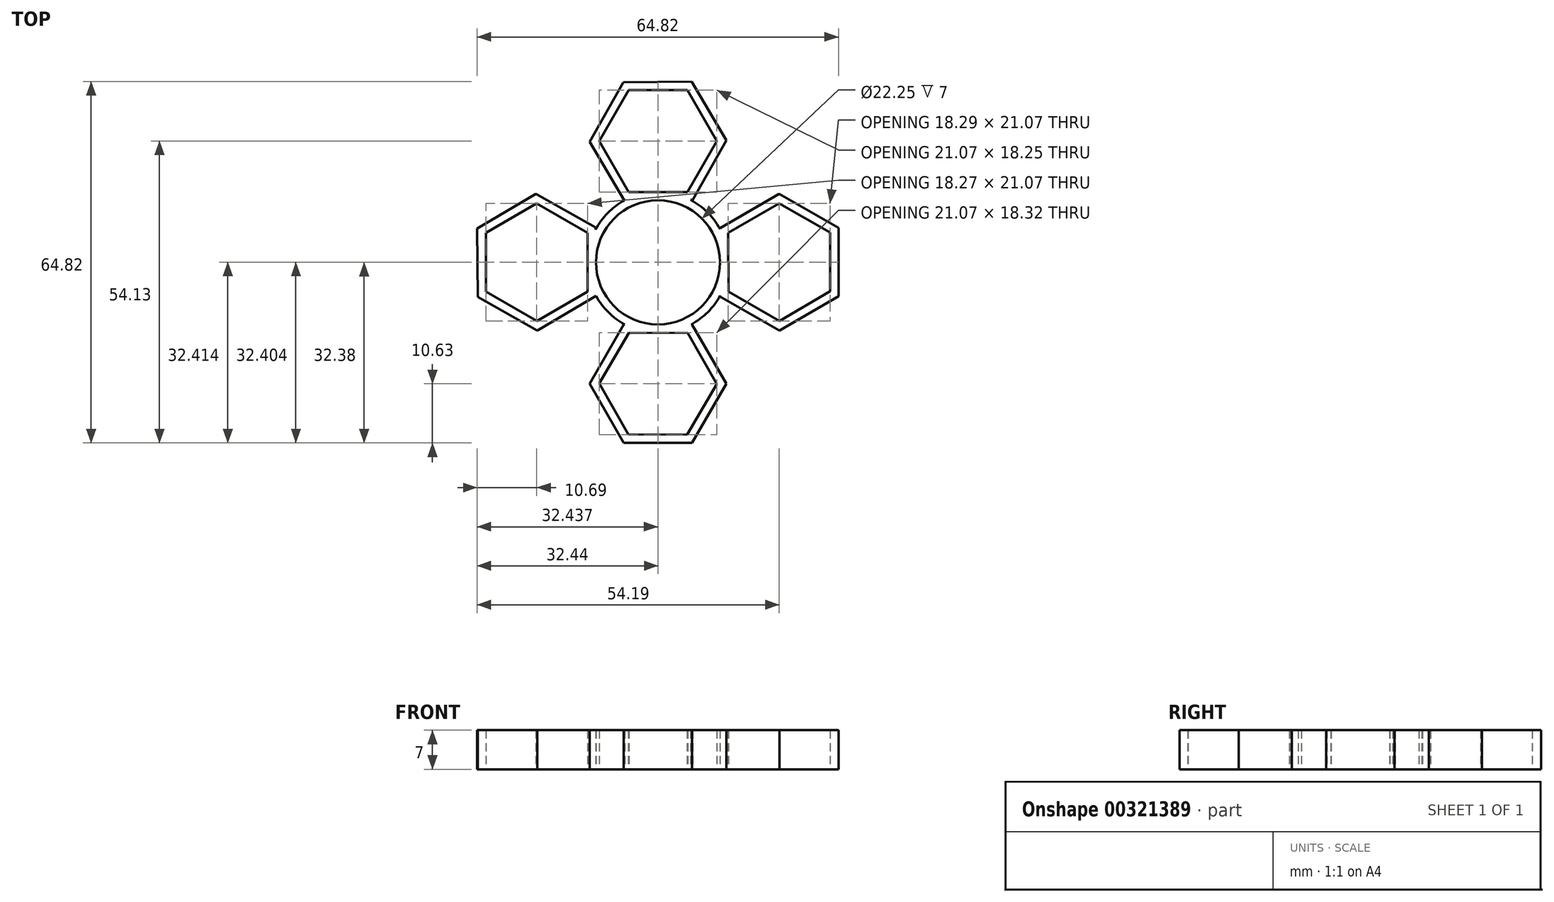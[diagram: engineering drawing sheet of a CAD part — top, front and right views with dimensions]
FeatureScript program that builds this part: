
annotation { "Feature Type Name" : "Feature", "Feature Type Description" : "" }
export const myFeature = defineFeature(function(context is Context, id is Id, definition is map)
    precondition{}
    {
        {
            var Q0;
            Q0=qCreatedBy(makeId("Top.planeOp"),FACE);
            var sketch = newSketch(context, id + "F0", { "sketchPlane" : qUnion([Q0])});
            skCircle(sketch, "E0", {"center": v(0, 0) * mm, "radius": 11.12 * mm});
            skCircle(sketch, "E1", {"center": v(0, 0) * mm, "radius": 12.62 * mm});
            skPoint(sketch, "E2", {"position": v(0, 12.63) * mm});
            skPoint(sketch, "E3", {"position": v(0, 21.75) * mm});
            skCircle(sketch, "E4", {"center": v(0, 21.75) * mm, "radius": 9.12 * mm, "construction": true});
            skPoint(sketch, "E5", {"position": v(0.1, 11.12) * mm});
            skLineSegment(sketch, "E6.0", {"start": v(5.27, 12.63) * mm, "end": v(-5.27, 12.63) * mm});
            skLineSegment(sketch, "E6.1", {"start": v(-5.27, 12.63) * mm, "end": v(-10.54, 21.75) * mm});
            skLineSegment(sketch, "E6.2", {"start": v(-10.54, 21.75) * mm, "end": v(-5.27, 30.88) * mm});
            skLineSegment(sketch, "E6.3", {"start": v(-5.27, 30.88) * mm, "end": v(5.27, 30.88) * mm});
            skLineSegment(sketch, "E6.4", {"start": v(5.27, 30.88) * mm, "end": v(10.54, 21.75) * mm});
            skLineSegment(sketch, "E6.5", {"start": v(10.54, 21.75) * mm, "end": v(5.27, 12.63) * mm});
            skCircle(sketch, "E7.cCircle", {"center": v(0, 21.75) * mm, "radius": 10.63 * mm, "construction": true});
            skLineSegment(sketch, "E7.0", {"start": v(6.24, 11.19) * mm, "end": v(-6.03, 11.06) * mm});
            skLineSegment(sketch, "E7.1", {"start": v(-6.03, 11.06) * mm, "end": v(-12.27, 21.63) * mm});
            skLineSegment(sketch, "E7.2", {"start": v(-12.27, 21.63) * mm, "end": v(-6.24, 32.31) * mm});
            skLineSegment(sketch, "E7.3", {"start": v(-6.24, 32.31) * mm, "end": v(6.03, 32.44) * mm});
            skLineSegment(sketch, "E7.4", {"start": v(6.03, 32.44) * mm, "end": v(12.27, 21.87) * mm});
            skLineSegment(sketch, "E7.5", {"start": v(12.27, 21.87) * mm, "end": v(6.24, 11.19) * mm});
            skPoint(sketch, "E8", {"position": v(11.12, 0.02) * mm});
            skPoint(sketch, "E9", {"position": v(12.62, 0) * mm});
            skPoint(sketch, "E10", {"position": v(21.75, 0.03) * mm});
            skCircle(sketch, "E11", {"center": v(21.75, 0.03) * mm, "radius": 9.13 * mm, "construction": true});
            skLineSegment(sketch, "E12.0", {"start": v(12.64, -5.27) * mm, "end": v(12.6, 5.27) * mm});
            skLineSegment(sketch, "E12.1", {"start": v(12.6, 5.27) * mm, "end": v(21.71, 10.57) * mm});
            skLineSegment(sketch, "E12.2", {"start": v(21.71, 10.57) * mm, "end": v(30.86, 5.34) * mm});
            skLineSegment(sketch, "E12.3", {"start": v(30.86, 5.34) * mm, "end": v(30.9, -5.2) * mm});
            skLineSegment(sketch, "E12.4", {"start": v(30.9, -5.2) * mm, "end": v(21.79, -10.5) * mm});
            skLineSegment(sketch, "E12.5", {"start": v(21.79, -10.5) * mm, "end": v(12.64, -5.27) * mm});
            skCircle(sketch, "E13.cCircle", {"center": v(21.75, 0.03) * mm, "radius": 10.63 * mm, "construction": true});
            skLineSegment(sketch, "E13.0", {"start": v(11.13, -6.12) * mm, "end": v(11.12, 6.15) * mm});
            skLineSegment(sketch, "E13.1", {"start": v(11.12, 6.15) * mm, "end": v(21.73, 12.3) * mm});
            skLineSegment(sketch, "E13.2", {"start": v(21.73, 12.3) * mm, "end": v(32.37, 6.19) * mm});
            skLineSegment(sketch, "E13.3", {"start": v(32.37, 6.19) * mm, "end": v(32.38, -6.08) * mm});
            skLineSegment(sketch, "E13.4", {"start": v(32.38, -6.08) * mm, "end": v(21.77, -12.23) * mm});
            skLineSegment(sketch, "E13.5", {"start": v(21.77, -12.23) * mm, "end": v(11.13, -6.12) * mm});
            skPoint(sketch, "E14", {"position": v(0, -11.12) * mm});
            skPoint(sketch, "E15", {"position": v(0.06, -12.62) * mm});
            skPoint(sketch, "E16", {"position": v(0, -21.75) * mm});
            skCircle(sketch, "E17", {"center": v(0, -21.75) * mm, "radius": 9.12 * mm, "construction": true});
            skCircle(sketch, "E18.cCircle", {"center": v(0, -21.75) * mm, "radius": 9.13 * mm, "construction": true});
            skLineSegment(sketch, "E18.0", {"start": v(-5.2, -12.59) * mm, "end": v(5.33, -12.66) * mm});
            skLineSegment(sketch, "E18.1", {"start": v(5.33, -12.66) * mm, "end": v(10.53, -21.82) * mm});
            skLineSegment(sketch, "E18.2", {"start": v(10.53, -21.82) * mm, "end": v(5.2, -30.91) * mm});
            skLineSegment(sketch, "E18.3", {"start": v(5.2, -30.91) * mm, "end": v(-5.33, -30.84) * mm});
            skLineSegment(sketch, "E18.4", {"start": v(-5.33, -30.84) * mm, "end": v(-10.54, -21.68) * mm});
            skLineSegment(sketch, "E18.5", {"start": v(-10.54, -21.68) * mm, "end": v(-5.2, -12.59) * mm});
            skCircle(sketch, "E19.cCircle", {"center": v(0, -21.75) * mm, "radius": 10.62 * mm, "construction": true});
            skLineSegment(sketch, "E19.0", {"start": v(-6.13, -11.12) * mm, "end": v(6.13, -11.13) * mm});
            skLineSegment(sketch, "E19.1", {"start": v(6.13, -11.13) * mm, "end": v(12.27, -21.75) * mm});
            skLineSegment(sketch, "E19.2", {"start": v(12.27, -21.75) * mm, "end": v(6.13, -32.38) * mm});
            skLineSegment(sketch, "E19.3", {"start": v(6.13, -32.38) * mm, "end": v(-6.14, -32.37) * mm});
            skLineSegment(sketch, "E19.4", {"start": v(-6.14, -32.37) * mm, "end": v(-12.27, -21.75) * mm});
            skLineSegment(sketch, "E19.5", {"start": v(-12.27, -21.75) * mm, "end": v(-6.13, -11.12) * mm});
            skPoint(sketch, "E20", {"position": v(-11.12, 0.13) * mm});
            skPoint(sketch, "E21", {"position": v(-12.62, 0.04) * mm});
            skCircle(sketch, "E22", {"center": v(-21.75, 0.02) * mm, "radius": 9.12 * mm, "construction": true});
            skCircle(sketch, "E23.cCircle", {"center": v(-21.75, 0.02) * mm, "radius": 9.13 * mm, "construction": true});
            skLineSegment(sketch, "E24.0", {"start": v(-12.63, 5.3) * mm, "end": v(-12.62, -5.23) * mm});
            skLineSegment(sketch, "E24.1", {"start": v(-12.62, -5.23) * mm, "end": v(-21.73, -10.51) * mm});
            skLineSegment(sketch, "E24.2", {"start": v(-21.73, -10.51) * mm, "end": v(-30.87, -5.26) * mm});
            skLineSegment(sketch, "E24.3", {"start": v(-30.87, -5.26) * mm, "end": v(-30.88, 5.28) * mm});
            skLineSegment(sketch, "E24.4", {"start": v(-30.88, 5.28) * mm, "end": v(-21.77, 10.56) * mm});
            skLineSegment(sketch, "E24.5", {"start": v(-21.77, 10.56) * mm, "end": v(-12.63, 5.3) * mm});
            skCircle(sketch, "E25.cCircle", {"center": v(-21.75, 0.02) * mm, "radius": 10.63 * mm, "construction": true});
            skLineSegment(sketch, "E25.0", {"start": v(-11.19, 6.26) * mm, "end": v(-11.06, -6) * mm});
            skLineSegment(sketch, "E25.1", {"start": v(-11.06, -6) * mm, "end": v(-21.63, -12.25) * mm});
            skLineSegment(sketch, "E25.2", {"start": v(-21.63, -12.25) * mm, "end": v(-32.31, -6.22) * mm});
            skLineSegment(sketch, "E25.3", {"start": v(-32.31, -6.22) * mm, "end": v(-32.44, 6.05) * mm});
            skLineSegment(sketch, "E25.4", {"start": v(-32.44, 6.05) * mm, "end": v(-21.87, 12.3) * mm});
            skLineSegment(sketch, "E25.5", {"start": v(-21.87, 12.3) * mm, "end": v(-11.19, 6.26) * mm});
            skSolve(sketch);
        }
        {
            var Q0;
            Q0 = qSketchRegion(id + "F0", true);
            extrude(context, id + "F1", {"entities" : qUnion([Q0]), "depth" : 7 * mm});
        }
    });
